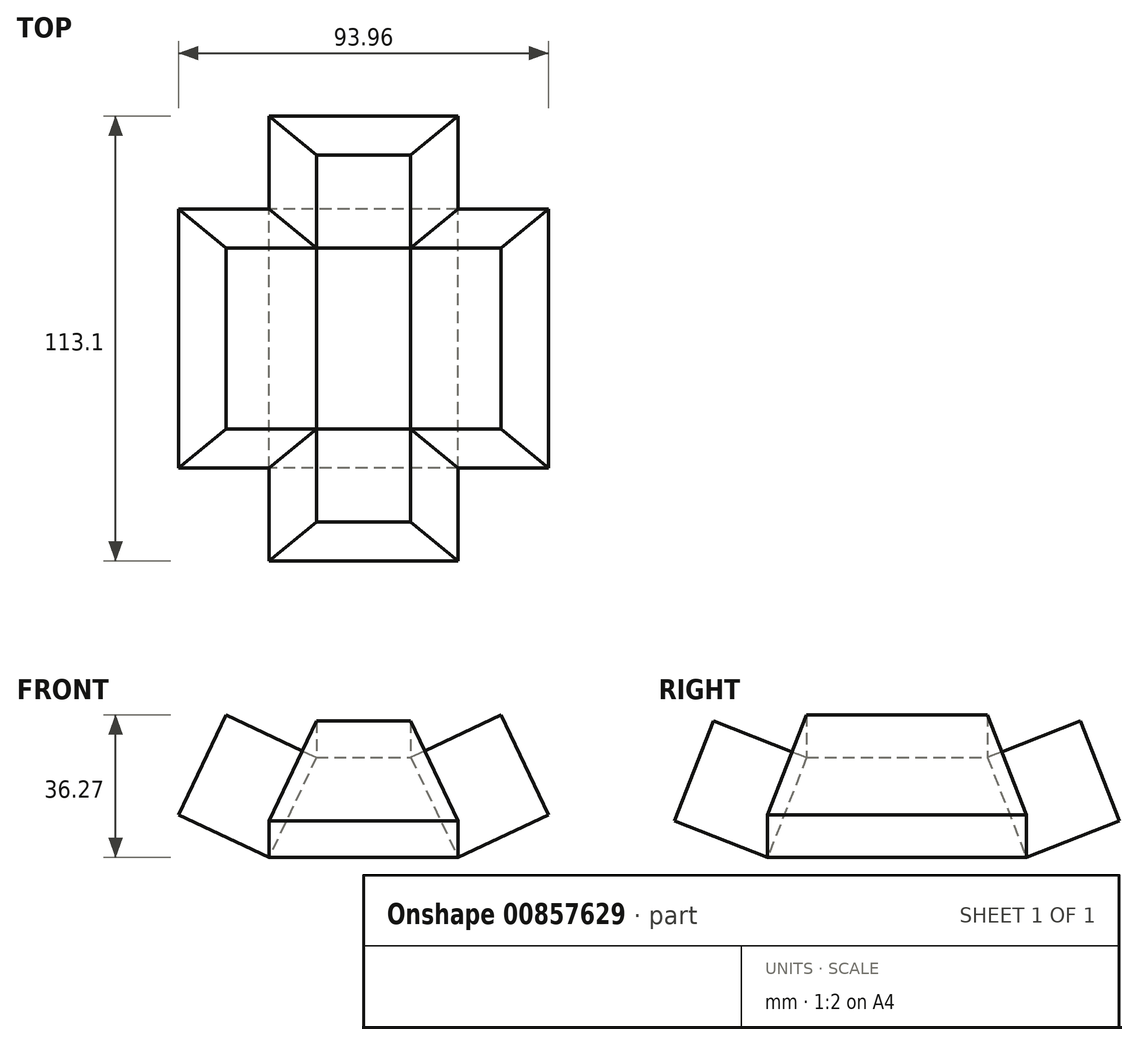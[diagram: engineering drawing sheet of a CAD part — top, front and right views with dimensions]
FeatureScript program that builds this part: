
annotation { "Feature Type Name" : "Feature", "Feature Type Description" : "" }
export const myFeature = defineFeature(function(context is Context, id is Id, definition is map)
    precondition{}
    {
        {
            var Q0;
            Q0=qCreatedBy(makeId("Top.planeOp"),FACE);
            var sketch = newSketch(context, id + "F0", { "sketchPlane" : qUnion([Q0])});
            skLineSegment(sketch, "E0.bottom", {"start": v(24.02, -32.89) * mm, "end": v(-24.02, -32.89) * mm});
            skLineSegment(sketch, "E0.top", {"start": v(24.02, 32.89) * mm, "end": v(-24.02, 32.89) * mm});
            skLineSegment(sketch, "E0.left", {"start": v(24.02, -32.89) * mm, "end": v(24.02, 32.89) * mm});
            skLineSegment(sketch, "E0.right", {"start": v(-24.02, -32.89) * mm, "end": v(-24.02, 32.89) * mm});
            skPoint(sketch, "E0.middle", {"position": v(0, 0) * mm});
            skSolve(sketch);
        }
        {
            var Q0;
            Q0=qCreatedBy(makeId("Top.planeOp"),FACE);
            var sketch = newSketch(context, id + "F1", { "sketchPlane" : qUnion([Q0])});
            skLineSegment(sketch, "E1.bottom", {"start": v(-12, -22.96) * mm, "end": v(12, -22.96) * mm});
            skLineSegment(sketch, "E1.top", {"start": v(-12, 22.96) * mm, "end": v(12, 22.96) * mm});
            skLineSegment(sketch, "E1.left", {"start": v(-12, -22.96) * mm, "end": v(-12, 22.96) * mm});
            skLineSegment(sketch, "E1.right", {"start": v(12, -22.96) * mm, "end": v(12, 22.96) * mm});
            skPoint(sketch, "E1.middle", {"position": v(0, 0) * mm});
            skSolve(sketch);
        }
        {
            var Q0;
            Q0=makeQuery(id+"F1.imprint","IMPRINT",FACE,{"disambiguationData":[TD([[makeQuery(id+"F1.imprint","IMPRINT",EDGE,{"derivedFrom":sQuery(id+"F1.wireOp",EDGE,"E1.bottom")}),1.0]])]});
            extrude(context, id + "F2", {"entities" : qUnion([Q0]), "depth" : 25.4 * mm, "offsetDistance" : 25.4 * mm});
        }
        {
            var Q1;
            Q1=makeQuery(id+"F2.opExtrude","CAP_FACE",FACE,{"disambiguationData":[OSD([sQuery(id+"F1.wireOp",EDGE,"E1.bottom"),sQuery(id+"F1.wireOp",EDGE,"E1.top"),sQuery(id+"F1.wireOp",EDGE,"E1.left"),sQuery(id+"F1.wireOp",EDGE,"E1.right")])],"isStart":false});
            var Q2;
            Q2=makeQuery(id+"F0.imprint","IMPRINT",FACE,{"disambiguationData":[TD([[makeQuery(id+"F0.imprint","IMPRINT",EDGE,{"derivedFrom":sQuery(id+"F0.wireOp",EDGE,"E0.bottom")}),-1.0]])]});
            loft(context, id + "F3", {"operationType" : NewBodyOperationType.ADD, "sheetProfilesArray" : [{ "sheetProfileEntities" : qUnion([Q1]) }, { "sheetProfileEntities" : qUnion([Q2]) }]});
        }
        {
            var Q0;
            Q0=makeQuery(id+"F3.opLoft","SWEPT_FACE",FACE,{"disambiguationData":[OSD([sQuery(id+"F0.wireOp",EDGE,"E0.top"),sQuery(id+"F0.wireOp",EDGE,"E0.left"),sQuery(id+"F0.wireOp",EDGE,"E0.right"),sQuery(id+"F1.wireOp",EDGE,"E1.top"),sQuery(id+"F1.wireOp",EDGE,"E1.left"),sQuery(id+"F1.wireOp",EDGE,"E1.right")])]});
            extrude(context, id + "F4", {"entities" : qUnion([Q0]), "operationType" : NewBodyOperationType.ADD, "depth" : 25.4 * mm, "offsetDistance" : 25.4 * mm});
        }
        {
            var Q0;
            Q0=makeQuery(id+"F3.opLoft","SWEPT_FACE",FACE,{"disambiguationData":[OSD([sQuery(id+"F0.wireOp",EDGE,"E0.bottom"),sQuery(id+"F0.wireOp",EDGE,"E0.left"),sQuery(id+"F0.wireOp",EDGE,"E0.right"),sQuery(id+"F1.wireOp",EDGE,"E1.bottom"),sQuery(id+"F1.wireOp",EDGE,"E1.left"),sQuery(id+"F1.wireOp",EDGE,"E1.right")])]});
            extrude(context, id + "F5", {"entities" : qUnion([Q0]), "operationType" : NewBodyOperationType.ADD, "depth" : 25.4 * mm, "offsetDistance" : 25.4 * mm});
        }
        {
            var Q0;
            Q0=makeQuery(id+"F3.opLoft","SWEPT_FACE",FACE,{"disambiguationData":[OSD([sQuery(id+"F0.wireOp",EDGE,"E0.bottom"),sQuery(id+"F0.wireOp",EDGE,"E0.top"),sQuery(id+"F0.wireOp",EDGE,"E0.left"),sQuery(id+"F1.wireOp",EDGE,"E1.bottom"),sQuery(id+"F1.wireOp",EDGE,"E1.top"),sQuery(id+"F1.wireOp",EDGE,"E1.right")])]});
            var sketch = newSketch(context, id + "F6", { "sketchPlane" : qUnion([Q0])});
            skSolve(sketch);
        }
        {
            var Q0;
            {var subQ0=sQuery(id+"F0.wireOp",EDGE,"E0.left");var subQ1=sQuery(id+"F0.wireOp",EDGE,"E0.top");var subQ2=sQuery(id+"F0.wireOp",EDGE,"E0.bottom");Q0=makeQuery(id+"F6.imprint","IMPRINT",FACE,{"disambiguationData":[TD([[makeQuery(id+"F6.imprint","IMPRINT",EDGE,{"derivedFrom":makeQuery(id+"F3.opLoft","MID_CAP_EDGE",EDGE,{"disambiguationData":[OSD([subQ2,subQ1,subQ0])],"capPos":1.0})}),-1.0]])]});}
            extrude(context, id + "F7", {"entities" : qUnion([Q0]), "operationType" : NewBodyOperationType.ADD, "depth" : 25.4 * mm, "offsetDistance" : 25.4 * mm});
        }
        {
            var Q0;
            Q0=makeQuery(id+"F3.opLoft","SWEPT_FACE",FACE,{"disambiguationData":[OSD([sQuery(id+"F0.wireOp",EDGE,"E0.bottom"),sQuery(id+"F0.wireOp",EDGE,"E0.top"),sQuery(id+"F0.wireOp",EDGE,"E0.right"),sQuery(id+"F1.wireOp",EDGE,"E1.bottom"),sQuery(id+"F1.wireOp",EDGE,"E1.top"),sQuery(id+"F1.wireOp",EDGE,"E1.left")])]});
            extrude(context, id + "F8", {"entities" : qUnion([Q0]), "operationType" : NewBodyOperationType.ADD, "depth" : 25.4 * mm, "offsetDistance" : 25.4 * mm});
        }
    });
